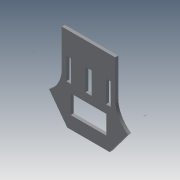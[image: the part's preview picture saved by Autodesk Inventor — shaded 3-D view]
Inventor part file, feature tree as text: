
AUTODESK INVENTOR PART (.ipt)
format: ipt  version: 2013 (Build 170138000, 138)  size: 1,185,792 bytes
history: native  units: mm
features: sketch x102, extrude x91, fillet x2
ambient origin geometry x8: Origin, YZ Plane, XZ Plane, XY Plane, X Axis, Y Axis, Z Axis, Center Point
bodies: Solid1 (feature_tree)
feature tree (195):
  extrude  "Extrusion1"  Depth=10.0mm
  extrude  "Extrusion2"  Depth=10.0mm
  sketch  "Sketch3"  dims[d8=2.0mm d9=0.0mm d11=3.0mm]
  extrude  "Extrusion3"  Depth=3.0mm
  extrude  "Extrusion4"  Depth=3.0mm
  extrude  "Extrusion5"  Depth=10.0mm TaperAngle=0.0deg
  extrude  "Extrusion6"  Depth=3.0mm
  sketch  "Sketch8"  dims[d24=10.0mm d25=0.0mm d26=2.0mm d27=0.0mm]
  extrude  "Extrusion7"  Depth=3.0mm
  extrude  "Extrusion8"  Depth=2.0mm TaperAngle=0.0deg
  extrude  "Extrusion9"  Depth=3.0mm
  extrude  "Extrusion10"  Depth=2.0mm TaperAngle=0.0deg
  extrude  "Extrusion11"  Depth=4.0mm
  extrude  "Extrusion12"  Depth=4.0mm
  extrude  "Extrusion13"  Depth=1.8mm
  sketch  "Sketch16"  dims[d61=4.0mm d62=4.0mm]
  extrude  "Extrusion14"  Depth=4.0mm
  extrude  "Extrusion15"  Depth=12.0mm
  extrude  "Extrusion16"  Depth=4.0mm
  extrude  "Extrusion17"  Depth=16.0mm
  sketch  "Sketch21"  dims[d75=30.0mm d77=2.0mm d78=0.0mm]
  extrude  "Extrusion18"  Depth=10.4mm
  extrude  "Extrusion19"  Depth=4.0mm
  extrude  "Extrusion20"  Depth=20.0mm
  extrude  "Extrusion21"  Depth=2.0mm TaperAngle=0.0deg
  extrude  "Extrusion22"  Depth=2.3mm
  extrude  "Extrusion23"  Depth=24.0mm
  extrude  "Extrusion24"  Depth=2.0mm TaperAngle=0.0deg
  extrude  "Extrusion25"  Depth=3.0mm
  extrude  "Extrusion26"  Depth=2.0mm TaperAngle=0.0deg
  extrude  "Extrusion27"  Depth=2.0mm TaperAngle=0.0deg
  extrude  "Extrusion28"  Depth=4.0mm
  extrude  "Extrusion29"  Depth=3.0mm
  extrude  "Extrusion30"  Depth=3.0mm
  extrude  "Extrusion31"  Depth=3.0mm
  extrude  "Extrusion32"  Depth=4.0mm
  extrude  "Extrusion33"  Depth=3.0mm
  extrude  "Extrusion34"  Depth=2.0mm TaperAngle=0.0deg
  extrude  "Extrusion35"  Depth=2.3mm
  extrude  "Extrusion36"  Depth=4.0mm
  extrude  "Extrusion37"  Depth=2.3mm
  sketch  "Sketch42"  dims[d147=24.0mm d148=24.0mm]
  sketch  "Sketch43"  dims[d149=2.0mm d150=0.0mm d151=2.0mm d152=0.0mm]
  extrude  "Extrusion38"  Depth=2.0mm TaperAngle=0.0deg
  extrude  "Extrusion39"  Depth=2.0mm TaperAngle=0.0deg
  extrude  "Extrusion40"  Depth=20.0mm
  extrude  "Extrusion41"  Depth=20.0mm
  extrude  "Extrusion42"  Depth=24.0mm
  extrude  "Extrusion43"  Depth=2.0mm TaperAngle=0.0deg
  extrude  "Extrusion44"  Depth=3.0mm
  extrude  "Extrusion45"  Depth=20.0mm
  extrude  "Extrusion46"  Depth=2.0mm TaperAngle=0.0deg
  extrude  "Extrusion47"  Depth=3.0mm
  extrude  "Extrusion48"  Depth=3.0mm
  fillet  "Fillet1"  Radius=3.0mm
  extrude  "Extrusion49"  Depth=2.5mm
  fillet  "Fillet2"  Radius=2.0mm
  extrude  "Extrusion50"  Depth=12.5mm
  extrude  "Extrusion51"  Depth=2.5mm
  extrude  "Extrusion52"  Depth=20.0mm
  extrude  "Extrusion53"  Depth=25.0mm
  extrude  "Extrusion54"  Depth=2.0mm TaperAngle=0.0deg
  extrude  "Extrusion55"  Depth=1.5mm
  extrude  "Extrusion56"  Depth=20.0mm
  extrude  "Extrusion57"  Depth=20.0mm
  extrude  "Extrusion58"  Depth=24.0mm
  extrude  "Extrusion59"  Depth=3.4mm
  extrude  "Extrusion60"  Depth=3.0mm
  extrude  "Extrusion61"  Depth=3.0mm
  extrude  "Extrusion62"  Depth=2.0mm TaperAngle=0.0deg
  sketch  "Sketch67"  dims[d218=3.0mm d219=3.0mm]
  extrude  "Extrusion63"  Depth=17.0mm
  extrude  "Extrusion64"  Depth=2.0mm TaperAngle=0.0deg
  extrude  "Extrusion65"  Depth=14.4mm
  sketch  "Sketch71"  dims[d228=1.5mm d229=3.0mm]
  sketch  "Sketch72"  dims[d230=2.0mm d231=0.0mm d233=2.0mm d234=0.0mm]
  extrude  "Extrusion66"  Depth=1.5mm
  sketch  "Sketch73"  dims[d236=14.5mm d237=13.95mm]
  sketch  "Sketch74"  dims[d238=13.95mm d239=3.0mm]
  extrude  "Extrusion67"  Depth=3.0mm
  extrude  "Extrusion68"  Depth=2.0mm TaperAngle=0.0deg
  extrude  "Extrusion69"  Depth=1.5mm
  extrude  "Extrusion70"  Depth=14.4mm
  extrude  "Extrusion71"  Depth=3.0mm
  sketch  "Sketch80"  dims[d256=19.0mm d259=19.0mm]
  sketch  "Sketch81"  dims[d260=2.0mm d261=0.0mm d262=10.0mm]
  sketch  "Sketch82"  dims[d263=4.0mm d264=4.0mm]
  extrude  "Extrusion72"  Depth=2.0mm TaperAngle=0.0deg
  extrude  "Extrusion73"  Depth=13.95mm
  extrude  "Extrusion74"  Depth=3.0mm
  extrude  "Extrusion75"  Depth=2.0mm TaperAngle=0.0deg
  extrude  "Extrusion76"  Depth=14.4mm
  extrude  "Extrusion77"  Depth=2.0mm
  extrude  "Extrusion78"  Depth=4.0mm
  extrude  "Extrusion79"  Depth=2.0mm TaperAngle=0.0deg
  extrude  "Extrusion80"  Depth=19.0mm
  extrude  "Extrusion81"  Depth=10.0mm
  extrude  "Extrusion82"  Depth=4.0mm
  extrude  "Extrusion83"  Depth=2.0mm TaperAngle=0.0deg
  extrude  "Extrusion84"  Depth=2.0mm TaperAngle=0.0deg
  extrude  "Extrusion85"  Depth=2.0mm TaperAngle=0.0deg
  extrude  "Extrusion86"  Depth=10.0mm TaperAngle=0.0deg
  extrude  "Extrusion87"  Depth=0.5mm TaperAngle=0.0deg
  extrude  "Extrusion88"  Depth=1.5mm TaperAngle=0.0deg
  extrude  "Extrusion89"  Depth=10.4mm
  extrude  "Extrusion90"  Depth=16.0mm
  extrude  "Extrusion91"  Depth=1.5mm TaperAngle=0.0deg
  sketch  "Sketch1"  dims[d2=10.0mm d3=10.0mm]
  sketch  "Sketch2"  dims[d4=10.0mm d7=10.0mm]
  sketch  "Sketch4"  dims[d12=3.0mm d14=3.0mm]
  sketch  "Sketch5"  dims[d15=3.0mm d16=10.0mm d17=0.0mm]
  sketch  "Sketch6"  dims[d20=6.0mm d21=3.0mm]
  sketch  "Sketch7"  dims[d22=6.0mm d23=3.0mm]
  sketch  "Sketch9"  dims[d34=3.0mm d36=3.0mm]
  sketch  "Sketch10"  dims[d37=2.0mm d38=0.0mm d39=2.0mm d40=0.0mm]
  sketch  "Sketch11"  dims[d48=2.0mm d49=4.0mm]
  sketch  "Sketch12"  dims[d51=12.0mm d52=4.0mm]
  sketch  "Sketch13"  dims[d53=2.0mm d54=0.0mm d55=1.8mm]
  sketch  "Sketch14"  dims[d56=2.0mm d57=4.0mm]
  sketch  "Sketch15"  dims[d58=2.0mm d59=0.0mm d60=12.0mm]
  sketch  "Sketch17"  dims[d63=2.0mm d64=0.0mm d65=16.0mm]
  sketch  "Sketch18"  dims[d66=12.0mm d67=10.4mm]
  sketch  "Sketch19"  dims[d68=2.0mm d69=0.0mm d70=4.0mm]
  sketch  "Sketch20"  dims[d71=2.0mm d72=0.0mm d74=20.0mm]
  sketch  "Sketch22"  dims[d83=2.3mm d84=2.3mm]
  sketch  "Sketch23"  dims[d85=2.0mm d86=0.0mm d90=24.0mm]
  sketch  "Sketch24"  dims[d92=24.0mm d93=2.0mm d94=0.0mm]
  sketch  "Sketch25"  dims[d97=3.0mm d98=3.0mm]
  sketch  "Sketch26"  dims[d100=3.0mm d101=2.0mm d102=0.0mm]
  sketch  "Sketch27"  dims[d103=2.0mm d104=0.0mm d105=2.0mm d106=0.0mm]
  sketch  "Sketch28"  dims[d111=4.0mm d112=4.0mm]
  sketch  "Sketch29"  dims[d113=3.0mm d114=3.0mm]
  sketch  "Sketch30"  dims[d116=3.0mm d117=3.0mm]
  sketch  "Sketch31"  dims[d118=3.0mm d119=3.0mm]
  sketch  "Sketch32"  dims[d120=3.0mm d121=4.0mm]
  sketch  "Sketch33"  dims[d122=3.0mm d123=3.0mm]
  sketch  "Sketch34"  dims[d124=3.0mm d125=2.0mm d126=0.0mm]
  sketch  "Sketch35"  dims[d127=2.3mm d128=2.3mm]
  sketch  "Sketch36"  dims[d131=4.0mm d132=4.0mm]
  sketch  "Sketch37"  dims[d133=2.0mm d134=0.0mm d135=2.3mm]
  sketch  "Sketch38"  dims[d136=2.3mm d137=2.0mm d138=0.0mm]
  sketch  "Sketch39"  dims[d139=3.0mm d140=2.0mm d141=0.0mm]
  sketch  "Sketch40"  dims[d142=2.0mm d143=0.0mm d144=20.0mm]
  sketch  "Sketch41"  dims[d145=14.0mm d146=20.0mm]
  sketch  "Sketch44"  dims[d157=3.0mm d158=3.0mm]
  sketch  "Sketch45"  dims[d159=2.0mm d160=0.0mm d161=20.0mm]
  sketch  "Sketch46"  dims[d162=20.0mm d163=2.0mm d164=0.0mm]
  sketch  "Sketch47"  dims[d165=2.0mm d166=0.0mm d167=3.0mm]
  sketch  "Sketch48"  dims[d168=3.0mm d169=3.0mm d170=3.0mm]
  sketch  "Sketch49"  dims[d171=2.5mm d172=2.5mm d173=2.0mm d174=0.0mm]
  sketch  "Sketch50"  dims[d175=2.0mm d176=0.0mm d178=12.5mm]
  sketch  "Sketch51"  dims[d179=12.5mm d180=2.5mm]
  sketch  "Sketch52"  dims[d181=2.5mm d183=20.0mm]
  sketch  "Sketch53"  dims[d185=20.0mm d186=25.0mm]
  sketch  "Sketch54"  dims[d187=25.0mm d188=2.0mm d189=0.0mm]
  sketch  "Sketch55"  dims[d190=1.5mm d191=1.5mm]
  sketch  "Sketch56"  dims[d192=1.5mm d193=20.0mm]
  sketch  "Sketch57"  dims[d194=1.5mm d195=20.0mm]
  sketch  "Sketch58"  dims[d196=24.0mm d197=24.0mm]
  sketch  "Sketch59"  dims[d198=2.0mm d199=0.0mm d200=3.4mm]
  sketch  "Sketch60"  dims[d201=3.4mm d202=3.0mm]
  sketch  "Sketch61"  dims[d203=3.0mm d204=3.0mm]
  sketch  "Sketch62"  dims[d205=3.0mm d206=2.0mm d207=0.0mm]
  sketch  "Sketch63"  dims[d208=2.0mm d209=0.0mm d210=17.0mm]
  sketch  "Sketch64"  dims[d211=14.4mm d212=2.0mm d213=0.0mm]
  sketch  "Sketch65"  dims[d214=19.5mm d215=14.4mm]
  sketch  "Sketch66"  dims[d216=1.5mm d217=1.5mm]
  sketch  "Sketch68"  dims[d220=2.0mm d221=0.0mm d222=2.0mm d223=0.0mm]
  sketch  "Sketch69"  dims[d224=19.5mm d225=1.5mm]
  sketch  "Sketch70"  dims[d226=3.0mm d227=14.4mm]
  sketch  "Sketch75"  dims[d241=3.0mm d242=2.0mm d243=0.0mm]
  sketch  "Sketch76"  dims[d244=2.0mm d245=0.0mm d248=14.4mm]
  sketch  "Sketch77"  dims[d249=21.6mm d250=2.0mm]
  sketch  "Sketch78"  dims[d251=2.0mm d252=4.0mm]
  sketch  "Sketch79"  dims[d253=4.0mm d254=2.0mm d255=0.0mm]
  sketch  "Sketch83"  dims[d265=2.0mm d266=0.0mm d267=2.0mm d268=0.0mm]
  sketch  "Sketch84"  dims[d269=2.0mm d270=0.0mm d271=2.0mm d272=0.0mm]
  sketch  "Sketch85"  dims[d273=3.6mm d274=2.0mm d275=0.0mm]
  sketch  "Sketch86"  dims[d276=1.5mm d277=10.0mm d278=0.0mm]
  sketch  "Sketch87"  dims[d279=2.0mm d280=0.5mm d281=0.0mm]
  sketch  "Sketch88"  dims[d282=0.5mm d283=1.5mm d284=0.0mm]
  sketch  "Sketch89"  dims[d285=1.5mm d286=0.0mm d287=10.4mm]
  sketch  "Sketch90"  dims[d288=14.398895mm d289=16.0mm]
  sketch  "Sketch91"  dims[d290=1.5mm d291=0.0mm d292=1.5mm d293=0.0mm]
  sketch  "Sketch92"  dims[d294=10.0mm d295=0.0mm]
  sketch  "Sketch93"  dims[d296=10.0mm d297=0.0mm]
  sketch  "Sketch94"  dims[d298=10.0mm d299=0.0mm]
  sketch  "Sketch95"  dims[d300=20.0mm d301=0.0mm]
  sketch  "Sketch96"  dims[d306=1.5mm d307=0.0mm]
  sketch  "Sketch97"  dims[d308=4.0mm]
  sketch  "Sketch98"  dims[d309=7.0mm]
  sketch  "Sketch99"  dims[d310=16.0mm]
  sketch  "Sketch100"  dims[d311=3.0mm]
  sketch  "Sketch101"  dims[d312=7.0mm]
  sketch  "Sketch102"  dims[d313=16.0mm d314=1.5mm d315=0.0mm d316=5.0mm d317=1.5mm d318=0.0mm d319=1.5mm d320=10.0mm d321=0.0mm d322=7.0mm d323=7.0mm d324=4.0mm d325=7.0mm d326=4.0mm d327=7.0mm d328=4.0mm d329=1.5mm d330=0.0mm d331=4.0mm d332=4.129mm d333=7.0mm d335=3.072mm d336=7.0mm d337=15.0mm d338=1.5mm d339=0.0mm d341=1.5mm d342=0.0mm d343=0.5mm d344=7.0mm d345=18.0mm d346=7.0mm d347=1.5mm d348=0.0mm d349=7.0mm d351=7.0mm d353=1.5mm d354=0.0mm d359=8.3mm d360=11.6mm d361=23.6mm d362=12.4mm d363=1.5mm d364=0.0mm d365=27.9mm d366=0.4mm d367=1.5mm d368=0.0mm d370=0.3mm d371=0.3mm d372=1.5mm d373=0.0mm d374=10.0mm d375=0.0mm d376=10.0mm d377=0.0mm d386=0.2mm d387=0.2mm d388=0.2mm d389=0.2mm d390=0.2mm d391=0.2mm d392=0.2mm d393=0.2mm d394=1.5mm d395=0.0mm d396=0.2mm d397=0.2mm d398=1.5mm d399=0.0mm d400=0.5mm d401=0.0mm d402=5.0mm d403=5.0mm d404=1.5mm d405=0.0mm d406=6.3mm d407=12.6mm d408=3.0mm d409=3.0mm d410=1.5mm d411=0.0mm d412=0.2mm d413=0.2mm d414=0.2mm d415=1.5mm d416=0.0mm d421=0.01mm d422=1.5mm d423=0.0mm d424=6.3mm d425=6.3mm d426=0.2mm d427=0.2mm d428=1.5mm d429=0.0mm d430=1.5mm d431=0.0mm d432=6.3mm d433=0.2mm d434=1.5mm d435=0.0mm d436=1.5mm d437=0.0mm d438=2.0mm d439=4.0mm d441=2.0mm d442=4.0mm d443=2.0mm d444=0.0mm d445=0.5mm d446=0.0mm d447=0.5mm d448=0.0mm d449=2.0mm d450=0.0mm d451=4.5mm d452=3.0mm d453=4.5mm d454=3.0mm d459=0.2mm d460=0.2mm d461=0.2mm d462=0.2mm d463=0.2mm d464=0.2mm d465=2.0mm d466=0.0mm d467=0.2mm d468=0.2mm d469=2.0mm d470=0.0mm d471=3.0mm d472=14.5mm d473=4.0mm d474=14.5mm d475=3.0mm d476=14.5mm d477=2.0mm d478=0.0mm d479=2.0mm d480=0.0mm d481=0.2mm d482=0.2mm d483=4.0mm d484=14.5mm d485=2.0mm d486=0.0mm]
